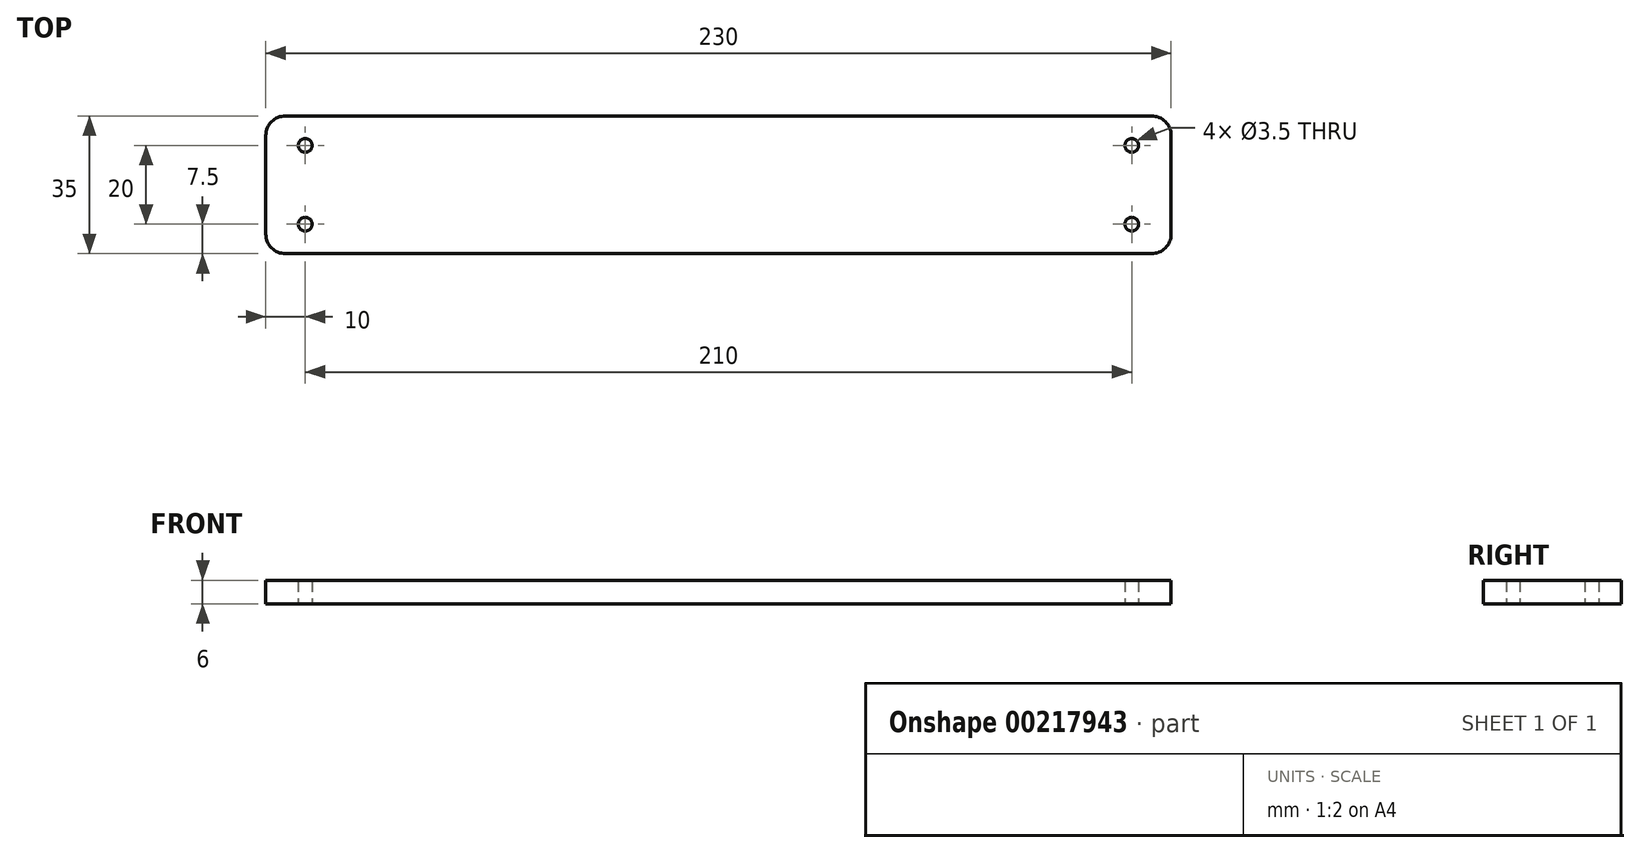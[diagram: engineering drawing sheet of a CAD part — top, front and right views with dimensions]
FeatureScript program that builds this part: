
annotation { "Feature Type Name" : "Feature", "Feature Type Description" : "" }
export const myFeature = defineFeature(function(context is Context, id is Id, definition is map)
    precondition{}
    {
        {
            var Q0;
            Q0=qCreatedBy(makeId("Top.planeOp"),FACE);
            var sketch = newSketch(context, id + "F0", { "sketchPlane" : qUnion([Q0])});
            skLineSegment(sketch, "E0.bottom", {"start": v(115, 17.5) * mm, "end": v(-115, 17.5) * mm});
            skLineSegment(sketch, "E0.top", {"start": v(115, -17.5) * mm, "end": v(-115, -17.5) * mm});
            skLineSegment(sketch, "E0.left", {"start": v(115, 17.5) * mm, "end": v(115, -17.5) * mm});
            skLineSegment(sketch, "E0.right", {"start": v(-115, 17.5) * mm, "end": v(-115, -17.5) * mm});
            skPoint(sketch, "E0.middle", {"position": v(0, 0) * mm});
            skLineSegment(sketch, "E1", {"start": v(-115, -17.5) * mm, "end": v(-115, -10) * mm, "construction": true});
            skLineSegment(sketch, "E2", {"start": v(-115, -10) * mm, "end": v(-105, -10) * mm, "construction": true});
            skLineSegment(sketch, "E3", {"start": v(-105, -10) * mm, "end": v(-105, 10) * mm, "construction": true});
            skCircle(sketch, "E4", {"center": v(-105, 10) * mm, "radius": 1.75 * mm});
            skCircle(sketch, "E5", {"center": v(-105, -10) * mm, "radius": 1.75 * mm});
            skCircle(sketch, "E6.MirrorC", {"center": v(105, 10) * mm, "radius": 1.75 * mm});
            skLineSegment(sketch, "E7", {"start": v(105, 10) * mm, "end": v(105, -10) * mm, "construction": true});
            skCircle(sketch, "E8", {"center": v(105, -10) * mm, "radius": 1.75 * mm});
            skSolve(sketch);
        }
        {
            var Q0;
            Q0=makeQuery(id+"F0.imprint","IMPRINT",FACE,{"disambiguationData":[TD([[makeQuery(id+"F0.imprint","IMPRINT",EDGE,{"derivedFrom":sQuery(id+"F0.wireOp",EDGE,"E0.bottom")}),1.0]])]});
            extrude(context, id + "F1", {"entities" : qUnion([Q0]), "endBound" : BoundingType.SYMMETRIC, "depth" : 6 * mm});
        }
        {
            var Q0;
            Q0=makeQuery(id+"F1.opExtrude","SWEPT_EDGE",EDGE,{"disambiguationData":[OSD([sQuery(id+"F0.wireOp",EDGE,"E0.bottom"),sQuery(id+"F0.wireOp",EDGE,"E0.right")])]});
            var Q1;
            Q1=makeQuery(id+"F1.opExtrude","SWEPT_EDGE",EDGE,{"disambiguationData":[OSD([sQuery(id+"F0.wireOp",EDGE,"E0.bottom"),sQuery(id+"F0.wireOp",EDGE,"E0.left")])]});
            var Q2;
            Q2=makeQuery(id+"F1.opExtrude","SWEPT_EDGE",EDGE,{"disambiguationData":[OSD([sQuery(id+"F0.wireOp",EDGE,"E0.top"),sQuery(id+"F0.wireOp",EDGE,"E0.left")])]});
            var Q3;
            Q3=makeQuery(id+"F1.opExtrude","SWEPT_EDGE",EDGE,{"disambiguationData":[OSD([sQuery(id+"F0.wireOp",EDGE,"E0.top"),sQuery(id+"F0.wireOp",EDGE,"E0.right")])]});
            fillet(context, id + "F2", {"entities" : qUnion([Q0, Q1, Q2, Q3]), "radius" : 5 * mm, "tangentPropagation" : true, "allowEdgeOverflow" : false});
        }
    });
